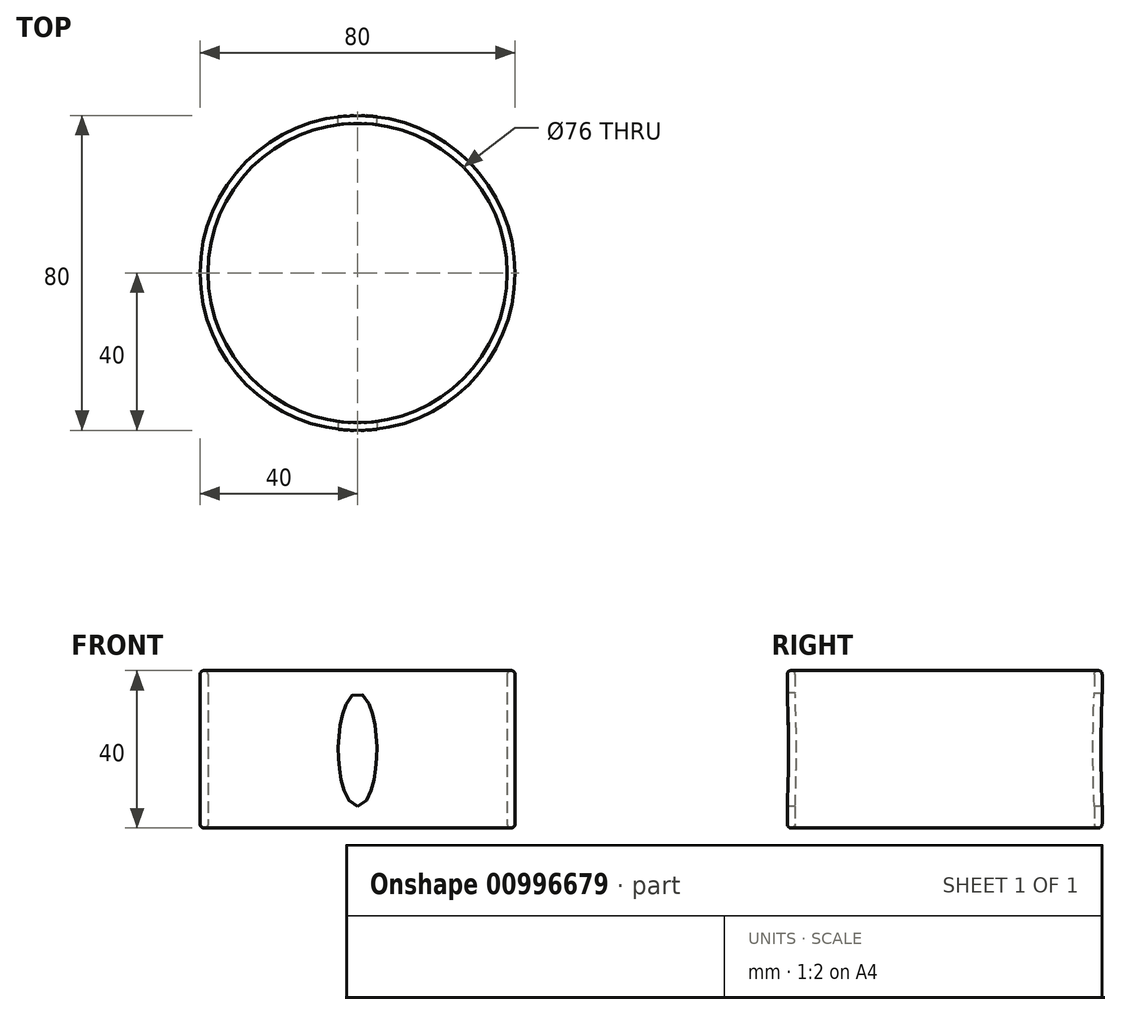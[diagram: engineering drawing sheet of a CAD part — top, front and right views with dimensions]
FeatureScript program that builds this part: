
annotation { "Feature Type Name" : "Feature", "Feature Type Description" : "" }
export const myFeature = defineFeature(function(context is Context, id is Id, definition is map)
    precondition{}
    {
        {
            var Q0;
            Q0=qCreatedBy(makeId("Top.planeOp"),FACE);
            var sketch = newSketch(context, id + "F0", { "sketchPlane" : qUnion([Q0])});
            skCircle(sketch, "E0", {"center": v(0, 0) * mm, "radius": 40 * mm});
            skCircle(sketch, "E1", {"center": v(0, 0) * mm, "radius": 38 * mm});
            skSolve(sketch);
        }
        {
            var Q0;
            Q0=makeQuery(id+"F0.imprint","IMPRINT",FACE,{"disambiguationData":[TD([[makeQuery(id+"F0.imprint","IMPRINT",EDGE,{"derivedFrom":sQuery(id+"F0.wireOp",EDGE,"E0")}),1.0]])]});
            extrude(context, id + "F1", {"entities" : qUnion([Q0]), "depth" : 40 * mm, "offsetDistance" : 25 * mm});
        }
        {
            var Q0;
            Q0=qCreatedBy(makeId("Front.planeOp"),FACE);
            var sketch = newSketch(context, id + "F2", { "sketchPlane" : qUnion([Q0])});
            skEllipse(sketch, "E2", {"center": v(0, 19.87) * mm, "majorRadius": 14.41 * mm, "minorRadius": 4.9 * mm, "majorAxis": v(0, -1)});
            skSolve(sketch);
        }
        {
            var Q0;
            Q0=makeQuery(id+"F2.imprint","IMPRINT",FACE,{"disambiguationData":[TD([[makeQuery(id+"F2.imprint","IMPRINT",EDGE,{"derivedFrom":sQuery(id+"F2.wireOp",EDGE,"E2")}),1.0]])]});
            var Q1;
            Q1=sQuery(id+"F2.wireOp",EDGE,"E2");
            extrude(context, id + "F3", {"entities" : qUnion([Q0]), "operationType" : NewBodyOperationType.REMOVE, "surfaceEntities" : qUnion([Q1]), "endBound" : BoundingType.THROUGH_ALL, "oppositeDirection" : true, "depth" : 25 * mm, "offsetDistance" : 25 * mm, "hasSecondDirection" : true, "secondDirectionBound" : SecondDirectionBoundingType.THROUGH_ALL, "secondDirectionOppositeDirection" : false, "secondDirectionDepth" : 25 * mm});
        }
        {
            var Q0;
            Q0=qCreatedBy(makeId("Front.planeOp"),FACE);
            var sketch = newSketch(context, id + "F4", { "sketchPlane" : qUnion([Q0])});
            skLineSegment(sketch, "E3", {"start": v(0, 60.5) * mm, "end": v(0, -30.64) * mm, "construction": true});
            skSolve(sketch);
        }
        {
            var Q0;
            Q0=makeQuery(id+"F1.opExtrude","CAP_FACE",FACE,{"disambiguationData":[OSD([sQuery(id+"F0.wireOp",EDGE,"E0"),sQuery(id+"F0.wireOp",EDGE,"E1")])],"isStart":false});
            var Q1;
            Q1=makeQuery(id+"F1.opExtrude","CAP_EDGE",EDGE,{"disambiguationData":[OSD([sQuery(id+"F0.wireOp",EDGE,"E1")])],"isStart":false});
            fillet(context, id + "F5", {"entities" : qUnion([Q0, Q1]), "radius" : 1 * mm, "tangentPropagation" : true, "allowEdgeOverflow" : false});
        }
        {
            var Q0;
            Q0=makeQuery(id+"F1.opExtrude","CAP_FACE",FACE,{"disambiguationData":[OSD([sQuery(id+"F0.wireOp",EDGE,"E0"),sQuery(id+"F0.wireOp",EDGE,"E1")])],"isStart":true});
            var Q1;
            Q1=makeQuery(id+"F1.opExtrude","CAP_EDGE",EDGE,{"disambiguationData":[OSD([sQuery(id+"F0.wireOp",EDGE,"E0")])],"isStart":true});
            var Q2;
            Q2=makeQuery(id+"F1.opExtrude","CAP_EDGE",EDGE,{"disambiguationData":[OSD([sQuery(id+"F0.wireOp",EDGE,"E1")])],"isStart":true});
            fillet(context, id + "F6", {"entities" : qUnion([Q0, Q1, Q2]), "radius" : 1 * mm, "tangentPropagation" : true, "allowEdgeOverflow" : false});
        }
    });
